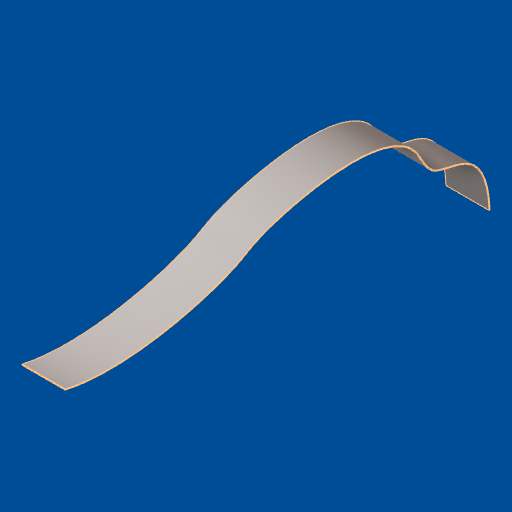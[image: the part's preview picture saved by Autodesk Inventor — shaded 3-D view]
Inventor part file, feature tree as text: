
AUTODESK INVENTOR PART (.ipt)
format: ipt  version: 2023.1 (Build 271208000, 208)  size: 105,472 bytes
history: mixed  units: in
note: dims shown in document units (in); Inventor stores cm internally (conversion verified against a paired STEP export)
features: other x1, sweep x1, imported_body x1
ambient origin geometry x8: Origin, YZ Plane, XZ Plane, XY Plane, X Axis, Y Axis, Z Axis, Center Point
bodies: Solid1 (imported_parasolid)
feature tree (3):
  other  "Plane1"
  sweep  "Sweep1"
  imported_body  NMx_Import_Brep_tag  [imported B-rep: ~5 faces, bbox_mm=None]
